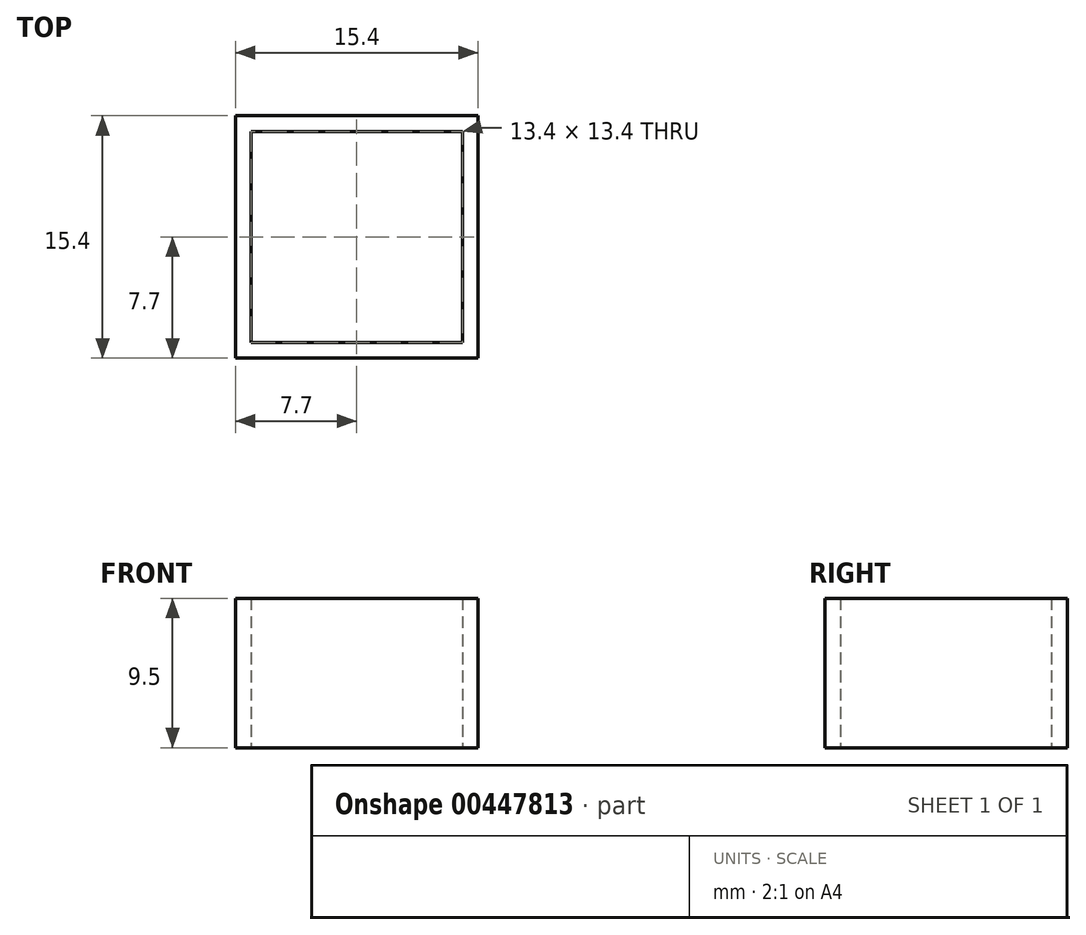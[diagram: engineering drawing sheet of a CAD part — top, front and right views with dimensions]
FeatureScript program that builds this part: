
annotation { "Feature Type Name" : "Feature", "Feature Type Description" : "" }
export const myFeature = defineFeature(function(context is Context, id is Id, definition is map)
    precondition{}
    {
        {
            var Q0;
            Q0=qCreatedBy(makeId("Top.planeOp"),FACE);
            var sketch = newSketch(context, id + "F0", { "sketchPlane" : qUnion([Q0])});
            skLineSegment(sketch, "E0.bottom", {"start": v(7.7, 7.7) * mm, "end": v(-7.7, 7.7) * mm});
            skLineSegment(sketch, "E0.top", {"start": v(7.7, -7.7) * mm, "end": v(-7.7, -7.7) * mm});
            skLineSegment(sketch, "E0.left", {"start": v(7.7, 7.7) * mm, "end": v(7.7, -7.7) * mm});
            skLineSegment(sketch, "E0.right", {"start": v(-7.7, 7.7) * mm, "end": v(-7.7, -7.7) * mm});
            skPoint(sketch, "E0.middle", {"position": v(0, 0) * mm});
            skLineSegment(sketch, "E1.bottom", {"start": v(6.7, 6.7) * mm, "end": v(-6.7, 6.7) * mm});
            skLineSegment(sketch, "E1.top", {"start": v(6.7, -6.7) * mm, "end": v(-6.7, -6.7) * mm});
            skLineSegment(sketch, "E1.left", {"start": v(6.7, 6.7) * mm, "end": v(6.7, -6.7) * mm});
            skLineSegment(sketch, "E1.right", {"start": v(-6.7, 6.7) * mm, "end": v(-6.7, -6.7) * mm});
            skSolve(sketch);
        }
        {
            var Q0;
            Q0 = qSketchRegion(id + "F0", true);
            extrude(context, id + "F1", {"entities" : qUnion([Q0]), "depth" : 9.5 * mm});
        }
    });
